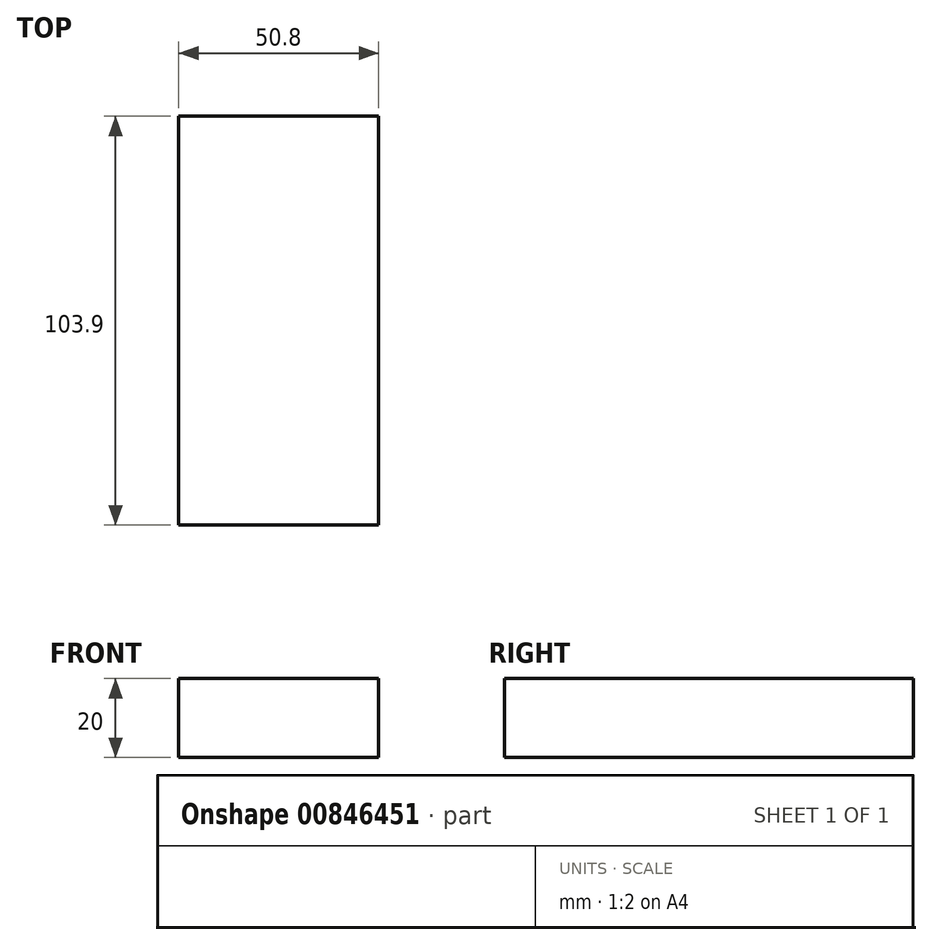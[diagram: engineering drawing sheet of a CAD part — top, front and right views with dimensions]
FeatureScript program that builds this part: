
annotation { "Feature Type Name" : "Feature", "Feature Type Description" : "" }
export const myFeature = defineFeature(function(context is Context, id is Id, definition is map)
    precondition{}
    {
        {
            var Q0;
            Q0=qCreatedBy(makeId("Right.planeOp"),FACE);
            var sketch = newSketch(context, id + "F0", { "sketchPlane" : qUnion([Q0])});
            skLineSegment(sketch, "E0", {"start": v(-51.09, 20) * mm, "end": v(52.81, 20) * mm});
            skLineSegment(sketch, "E1", {"start": v(52.81, 20) * mm, "end": v(52.81, 0) * mm});
            skLineSegment(sketch, "E2", {"start": v(52.81, 0) * mm, "end": v(-51.09, 0) * mm});
            skLineSegment(sketch, "E3", {"start": v(-51.09, 20) * mm, "end": v(-51.09, 0) * mm});
            skSolve(sketch);
        }
        {
            var Q0;
            Q0=makeQuery(id+"F0.imprint","IMPRINT",FACE,{"disambiguationData":[TD([[makeQuery(id+"F0.imprint","IMPRINT",EDGE,{"derivedFrom":sQuery(id+"F0.wireOp",EDGE,"E0")}),-1.0]])]});
            extrude(context, id + "F1", {"entities" : qUnion([Q0]), "depth" : 50.8 * mm, "offsetDistance" : 25.4 * mm});
        }
    });
